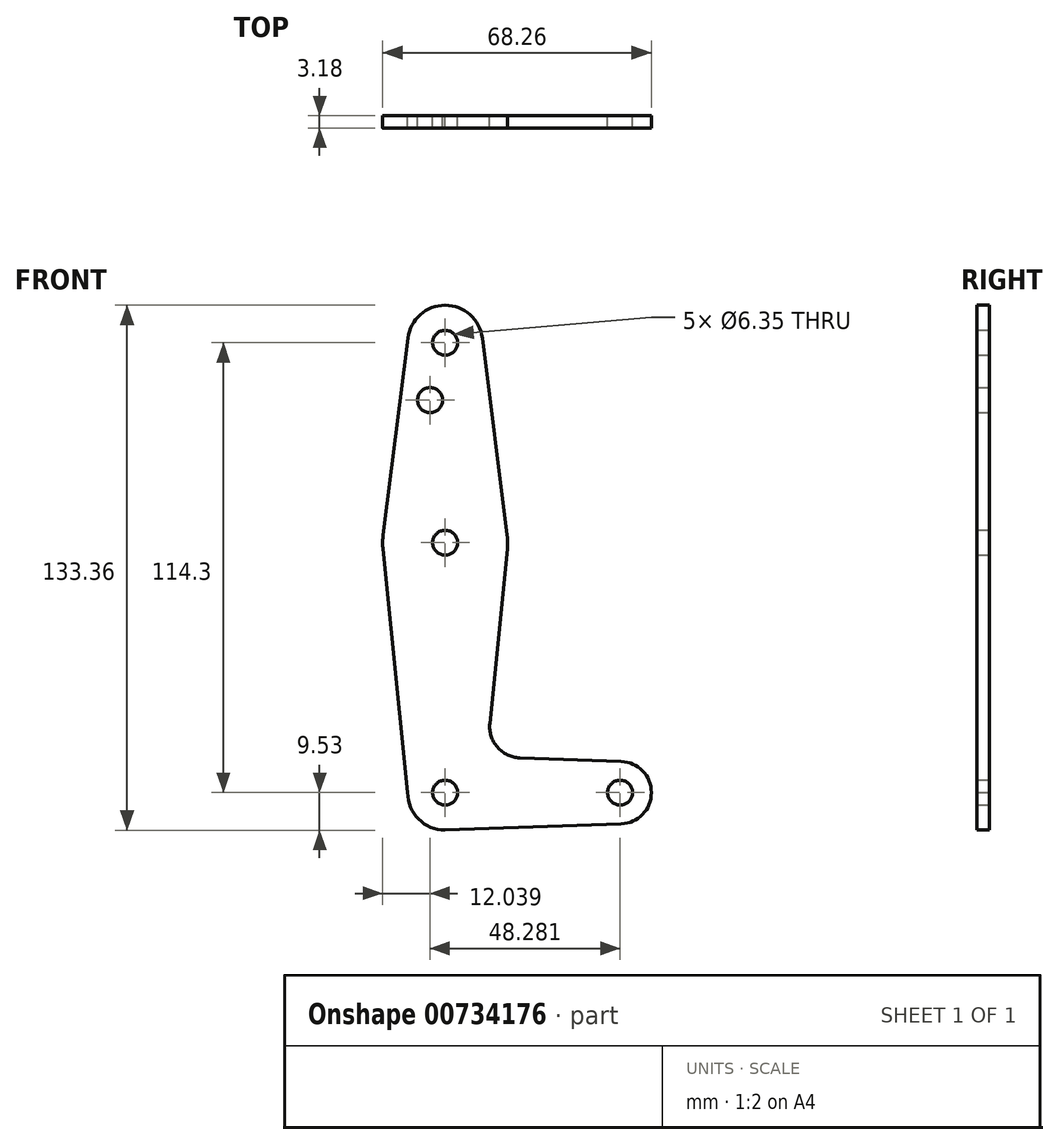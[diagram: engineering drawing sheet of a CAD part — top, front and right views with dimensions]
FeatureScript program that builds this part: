
annotation { "Feature Type Name" : "Feature", "Feature Type Description" : "" }
export const myFeature = defineFeature(function(context is Context, id is Id, definition is map)
    precondition{}
    {
        {
            var Q0;
            Q0=qCreatedBy(makeId("Front.planeOp"),FACE);
            var sketch = newSketch(context, id + "F0", { "sketchPlane" : qUnion([Q0])});
            skCircle(sketch, "E0", {"center": v(0, 0) * mm, "radius": 9.53 * mm});
            skLineSegment(sketch, "E1", {"start": v(0, 0) * mm, "end": v(0, 114.3) * mm});
            skCircle(sketch, "E2", {"center": v(0, 63.5) * mm, "radius": 15.88 * mm});
            skCircle(sketch, "E3", {"center": v(0, 114.3) * mm, "radius": 9.52 * mm});
            skLineSegment(sketch, "E4", {"start": v(0, 0) * mm, "end": v(44.45, 0) * mm, "construction": true});
            skCircle(sketch, "E5", {"center": v(44.45, 0) * mm, "radius": 7.94 * mm});
            skLineSegment(sketch, "E6", {"start": v(-9.45, 115.5) * mm, "end": v(-15.75, 65.48) * mm});
            skLineSegment(sketch, "E7", {"start": v(9.45, 115.5) * mm, "end": v(15.75, 65.48) * mm});
            skLineSegment(sketch, "E8", {"start": v(18.97, 8.85) * mm, "end": v(44.73, 7.93) * mm});
            skLineSegment(sketch, "E9", {"start": v(0, -9.53) * mm, "end": v(44.73, -7.93) * mm});
            skLineSegment(sketch, "E10", {"start": v(15.8, 61.91) * mm, "end": v(11.34, 17.59) * mm});
            skLineSegment(sketch, "E11", {"start": v(-9.52, 0) * mm, "end": v(-15.8, 61.91) * mm});
            skCircle(sketch, "E12", {"center": v(0, 63.5) * mm, "radius": 3.18 * mm});
            skCircle(sketch, "E13", {"center": v(0, 114.3) * mm, "radius": 3.18 * mm});
            skCircle(sketch, "E14", {"center": v(-3.83, 99.73) * mm, "radius": 3.18 * mm});
            skCircle(sketch, "E15", {"center": v(44.45, 0) * mm, "radius": 3.18 * mm});
            skCircle(sketch, "E16", {"center": v(0, 0) * mm, "radius": 3.18 * mm});
            skPoint(sketch, "E17.newPointB", {"position": v(9.57, 0) * mm});
            skArc(sketch, "E17.filletArc", {"start": v(11.34, 17.59) * mm, "mid": v(13.26, 11.57) * mm, "end": v(18.97, 8.85) * mm});
            skSolve(sketch);
        }
        {
            var Q0;
            {var subQ0=sQuery(id+"F0.wireOp",EDGE,"E6");Q0=makeQuery(id+"F0.imprint","IMPRINT",FACE,{"disambiguationData":[TD([[makeQuery(id+"F0.imprint","IMPRINT",EDGE,{"derivedFrom":subQ0}),1.0]])]});}
            var Q1;
            {var subQ5=sQuery(id+"F0.wireOp",EDGE,"E7");Q1=makeQuery(id+"F0.imprint","IMPRINT",FACE,{"disambiguationData":[TD([[makeQuery(id+"F0.imprint","IMPRINT",EDGE,{"derivedFrom":subQ5}),-1.0]])]});}
            var Q2;
            Q2=makeQuery(id+"F0.imprint","IMPRINT",FACE,{"disambiguationData":[TD([[makeQuery(id+"F0.imprint","IMPRINT",EDGE,{"derivedFrom":sQuery(id+"F0.wireOp",EDGE,"E13")}),-1.0]])]});
            var Q3;
            {var subQ0=sQuery(id+"F0.wireOp",EDGE,"E2");var subQ2=sQuery(id+"F0.wireOp",EDGE,"E1");var subQ3=makeQuery(id+"F0.imprint","INTERSECT",VERTEX,{"disambiguationData":[OD(0.0)],"derivedFrom":[subQ2,subQ0]});Q3=makeQuery(id+"F0.imprint","IMPRINT",FACE,{"disambiguationData":[TD([[makeQuery(id+"F0.imprint","IMPRINT",EDGE,{"disambiguationData":[TD([[subQ3,-1.0]])],"derivedFrom":subQ2}),-1.0]])]});}
            var Q4;
            {var subQ0=sQuery(id+"F0.wireOp",EDGE,"E2");var subQ4=sQuery(id+"F0.wireOp",EDGE,"E1");var subQ7=makeQuery(id+"F0.imprint","INTERSECT",VERTEX,{"disambiguationData":[OD(0.0)],"derivedFrom":[subQ4,subQ0]});Q4=makeQuery(id+"F0.imprint","IMPRINT",FACE,{"disambiguationData":[TD([[makeQuery(id+"F0.imprint","IMPRINT",EDGE,{"disambiguationData":[TD([[subQ7,-1.0]])],"derivedFrom":subQ4}),1.0]])]});}
            var Q5;
            {var subQ0=sQuery(id+"F0.wireOp",EDGE,"E11");Q5=makeQuery(id+"F0.imprint","IMPRINT",FACE,{"disambiguationData":[TD([[makeQuery(id+"F0.imprint","IMPRINT",EDGE,{"derivedFrom":subQ0}),-1.0]])]});}
            var Q6;
            {var subQ5=sQuery(id+"F0.wireOp",EDGE,"E8");Q6=makeQuery(id+"F0.imprint","IMPRINT",FACE,{"disambiguationData":[TD([[makeQuery(id+"F0.imprint","IMPRINT",EDGE,{"derivedFrom":subQ5}),-1.0]])]});}
            var Q7;
            Q7=makeQuery(id+"F0.imprint","IMPRINT",FACE,{"disambiguationData":[TD([[makeQuery(id+"F0.imprint","IMPRINT",EDGE,{"derivedFrom":sQuery(id+"F0.wireOp",EDGE,"E16")}),-1.0]])]});
            var Q8;
            Q8=makeQuery(id+"F0.imprint","IMPRINT",FACE,{"disambiguationData":[TD([[makeQuery(id+"F0.imprint","IMPRINT",EDGE,{"derivedFrom":sQuery(id+"F0.wireOp",EDGE,"E15")}),-1.0]])]});
            extrude(context, id + "F1", {"entities" : qUnion([Q0, Q1, Q2, Q3, Q4, Q5, Q6, Q7, Q8]), "depth" : 3.17 * mm, "offsetDistance" : 25.4 * mm});
        }
    });
